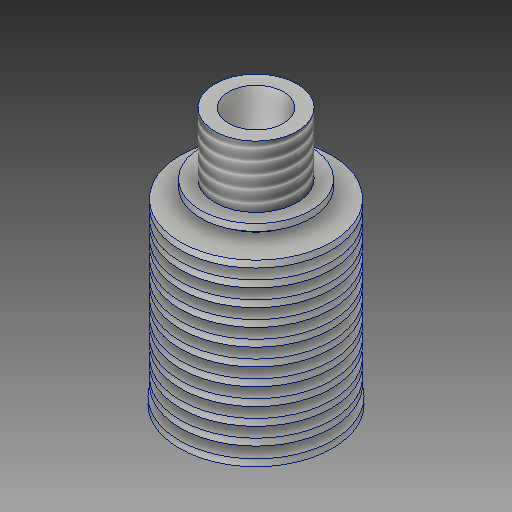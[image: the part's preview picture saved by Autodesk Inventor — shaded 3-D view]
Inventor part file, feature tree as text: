
AUTODESK INVENTOR PART (.ipt)
format: ipt  version: 2019 (Build 230136000, 136)  size: 275,456 bytes
history: native  units: mm
features: other x2, sketch x2, thread x1
ambient origin geometry x8: Origin, YZ Plane, XZ Plane, XY Plane, X Axis, Y Axis, Z Axis, Center Point
bodies: Solid1 (feature_tree)
feature tree (5):
  thread  "Threaded Heatsink.ipt"  [1 undecoded]
  other  "Solid1::Threaded Heatsink.ipt"
  other  "TaggingFeature1"
  sketch  "Sketch1"
  sketch  "Sketch2"
note: 1 required parameter value undecoded (feature->parameter linkage not recoverable at this tier; creation-order binding heuristic only, values carry confidence <= 0.55)
